# Revit family: Lighting-Recessed- Wall-Amerlux-Passo RT
name_source: partatom
category: Lighting Fixtures
revit_build: Autodesk Revit 2017 (Build: 20190508_0315(x64)
units: mm (PartAtom-declared; Revit-internal decimal feet)

## family parameters
Cut with Voids When Loaded = No
Host = Face
Light Source = Yes
Part Type = Normal
Room Calculation Point = No
Round Connector Dimension = Use Diameter
Shared = No

## types (2) — shared parameters
Apparent Load = 0 VA
Color Filter = 16777215
Default Elevation = 4' - 0"
Description = Recessed Steplight
Dimming Lamp Color Temperature Shift = <None>
Emit from Line Length = 4' - 0"
Height = 0' - 3"
Lamp = LED
Manufacturer = Amerlux
Model = Passo RT
Number of Poles = 1
Photometric Web File = Load File
Power Factor = 1
Tilt Angle = -90.00°
URL = http://www.amerlux.com
Voltage = 0 V
Width = 0' - 4"

## per-type parameters (varying)
| type | Length | Opening |
| PRCD8 | 0' - 8 1/2" | 0' - 4" |
| PRCD12 | 1' - 0 1/2" | 0' - 8" |

## geometry (parser evidence)
native form markers: Sweep x2
no freeform markers — native parametric forms only
